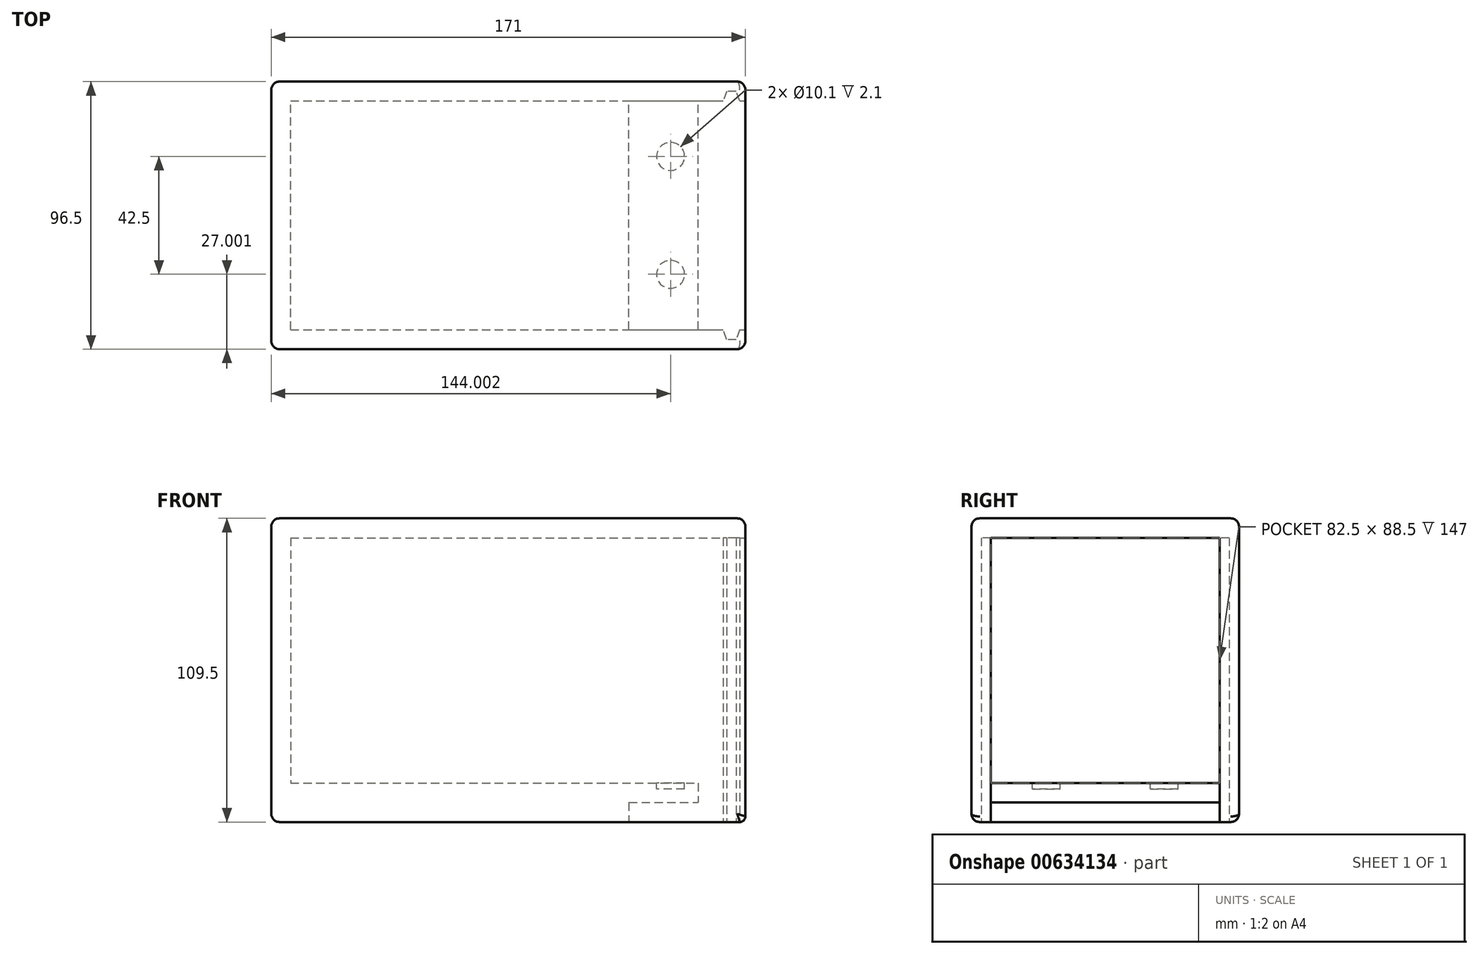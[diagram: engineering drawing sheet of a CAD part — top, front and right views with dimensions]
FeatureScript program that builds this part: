
annotation { "Feature Type Name" : "Feature", "Feature Type Description" : "" }
export const myFeature = defineFeature(function(context is Context, id is Id, definition is map)
    precondition{}
    {
        {
            var Q0;
            Q0=qCreatedBy(makeId("Top.planeOp"),FACE);
            var sketch = newSketch(context, id + "F0", { "sketchPlane" : qUnion([Q0])});
            skLineSegment(sketch, "E0.bottom", {"start": v(-82.1, 47.48) * mm, "end": v(81.9, 47.48) * mm});
            skLineSegment(sketch, "E0.top", {"start": v(-82.1, -49.02) * mm, "end": v(81.9, -49.02) * mm});
            skLineSegment(sketch, "E0.left", {"start": v(-82.1, 47.48) * mm, "end": v(-82.1, -49.02) * mm});
            skLineSegment(sketch, "E0.right", {"start": v(81.9, 47.48) * mm, "end": v(81.9, -49.02) * mm});
            skSolve(sketch);
        }
        {
            var Q0;
            Q0=makeQuery(id+"F0.imprint","IMPRINT",FACE,{"disambiguationData":[TD([[makeQuery(id+"F0.imprint","IMPRINT",EDGE,{"derivedFrom":sQuery(id+"F0.wireOp",EDGE,"E0.bottom")}),-1.0]])]});
            extrude(context, id + "F1", {"entities" : qUnion([Q0]), "depth" : 102.5 * mm, "offsetDistance" : 25 * mm});
        }
        {
            var Q0;
            Q0=makeQuery(id+"F1.opExtrude","CAP_FACE",FACE,{"disambiguationData":[OSD([sQuery(id+"F0.wireOp",EDGE,"E0.bottom"),sQuery(id+"F0.wireOp",EDGE,"E0.top"),sQuery(id+"F0.wireOp",EDGE,"E0.left"),sQuery(id+"F0.wireOp",EDGE,"E0.right")])],"isStart":false});
            var sketch = newSketch(context, id + "F2", { "sketchPlane" : qUnion([Q0])});
            skLineSegment(sketch, "E1.bottom", {"start": v(-75.1, 40.48) * mm, "end": v(74.9, 40.48) * mm});
            skLineSegment(sketch, "E1.top", {"start": v(-75.1, -42.02) * mm, "end": v(74.9, -42.02) * mm});
            skLineSegment(sketch, "E1.left", {"start": v(-75.1, 40.48) * mm, "end": v(-75.1, -42.02) * mm});
            skLineSegment(sketch, "E1.right", {"start": v(74.9, 40.48) * mm, "end": v(74.9, -42.02) * mm});
            skSolve(sketch);
        }
        {
            var Q0;
            Q0=makeQuery(id+"F1.opExtrude","SWEPT_FACE",FACE,{"disambiguationData":[OSD([sQuery(id+"F0.wireOp",EDGE,"E0.right")])]});
            var sketch = newSketch(context, id + "F3", { "sketchPlane" : qUnion([Q0])});
            skLineSegment(sketch, "E2.bottom", {"start": v(-42.02, 95.5) * mm, "end": v(40.48, 95.5) * mm});
            skLineSegment(sketch, "E2.top", {"start": v(-42.02, 7) * mm, "end": v(40.48, 7) * mm});
            skLineSegment(sketch, "E2.left", {"start": v(-42.02, 95.5) * mm, "end": v(-42.02, 7) * mm});
            skLineSegment(sketch, "E2.right", {"start": v(40.48, 95.5) * mm, "end": v(40.48, 7) * mm});
            skSolve(sketch);
        }
        {
            var Q0;
            Q0=makeQuery(id+"F3.imprint","IMPRINT",FACE,{"disambiguationData":[TD([[makeQuery(id+"F3.imprint","IMPRINT",EDGE,{"derivedFrom":sQuery(id+"F3.wireOp",EDGE,"E2.bottom")}),-1.0]])]});
            extrude(context, id + "F4", {"entities" : qUnion([Q0]), "operationType" : NewBodyOperationType.REMOVE, "oppositeDirection" : true, "depth" : 157 * mm, "offsetDistance" : 25 * mm});
        }
        {
            var Q0;
            Q0=makeQuery(id+"F1.opExtrude","CAP_FACE",FACE,{"disambiguationData":[OSD([sQuery(id+"F0.wireOp",EDGE,"E0.bottom"),sQuery(id+"F0.wireOp",EDGE,"E0.top"),sQuery(id+"F0.wireOp",EDGE,"E0.left"),sQuery(id+"F0.wireOp",EDGE,"E0.right")])],"isStart":true});
            var sketch = newSketch(context, id + "F5", { "sketchPlane" : qUnion([Q0])});
            skLineSegment(sketch, "E3.bottom", {"start": v(41.9, 42.02) * mm, "end": v(81.9, 42.02) * mm});
            skLineSegment(sketch, "E3.top", {"start": v(41.9, -40.48) * mm, "end": v(81.9, -40.48) * mm});
            skLineSegment(sketch, "E3.left", {"start": v(41.9, 42.02) * mm, "end": v(41.9, -40.48) * mm});
            skLineSegment(sketch, "E3.right", {"start": v(81.9, 42.02) * mm, "end": v(81.9, -40.48) * mm});
            skSolve(sketch);
        }
        {
            var Q0;
            Q0=makeQuery(id+"F5.imprint","IMPRINT",FACE,{"disambiguationData":[TD([[makeQuery(id+"F5.imprint","IMPRINT",EDGE,{"derivedFrom":sQuery(id+"F5.wireOp",EDGE,"E3.bottom")}),-1.0]])]});
            extrude(context, id + "F6", {"entities" : qUnion([Q0]), "operationType" : NewBodyOperationType.REMOVE, "oppositeDirection" : true, "depth" : 7 * mm, "offsetDistance" : 25 * mm});
        }
        {
            var Q0;
            Q0=makeQuery(id+"F1.opExtrude","CAP_FACE",FACE,{"disambiguationData":[OSD([sQuery(id+"F0.wireOp",EDGE,"E0.bottom"),sQuery(id+"F0.wireOp",EDGE,"E0.top"),sQuery(id+"F0.wireOp",EDGE,"E0.left"),sQuery(id+"F0.wireOp",EDGE,"E0.right")])],"isStart":true});
            extrude(context, id + "F7", {"entities" : qUnion([Q0]), "operationType" : NewBodyOperationType.ADD, "depth" : 7 * mm, "offsetDistance" : 25 * mm});
        }
        {
            var Q0;
            Q0=makeQuery(id+"F7.opExtrude","CAP_FACE",FACE,{"disambiguationData":[OSD([sQuery(id+"F0.wireOp",EDGE,"E0.bottom"),sQuery(id+"F0.wireOp",EDGE,"E0.top"),sQuery(id+"F0.wireOp",EDGE,"E0.left"),sQuery(id+"F0.wireOp",EDGE,"E0.right")])],"isStart":false});
            var sketch = newSketch(context, id + "F8", { "sketchPlane" : qUnion([Q0])});
            skLineSegment(sketch, "E4.bottom", {"start": v(11.9, 42.02) * mm, "end": v(41.9, 42.02) * mm});
            skLineSegment(sketch, "E4.top", {"start": v(11.9, -40.48) * mm, "end": v(41.9, -40.48) * mm});
            skLineSegment(sketch, "E4.left", {"start": v(11.9, 42.02) * mm, "end": v(11.9, -40.48) * mm});
            skLineSegment(sketch, "E4.right", {"start": v(41.9, 42.02) * mm, "end": v(41.9, -40.48) * mm});
            skSolve(sketch);
        }
        {
            var Q0;
            Q0=makeQuery(id+"F8.imprint","IMPRINT",FACE,{"disambiguationData":[TD([[makeQuery(id+"F8.imprint","IMPRINT",EDGE,{"derivedFrom":sQuery(id+"F8.wireOp",EDGE,"E4.bottom")}),-1.0]])]});
            extrude(context, id + "F9", {"entities" : qUnion([Q0]), "operationType" : NewBodyOperationType.REMOVE, "oppositeDirection" : true, "depth" : 7 * mm, "offsetDistance" : 25 * mm});
        }
        {
            var Q0;
            {var subQ0=sQuery(id+"F0.wireOp",EDGE,"E0.right");var subQ1=makeQuery(id+"F1.opExtrude","SWEPT_FACE",FACE,{"disambiguationData":[OSD([subQ0])]});var subQ2=sQuery(id+"F0.wireOp",EDGE,"E0.top");var subQ3=sQuery(id+"F0.wireOp",EDGE,"E0.bottom");var subQ5=makeQuery(id+"F1.opExtrude","CAP_EDGE",EDGE,{"disambiguationData":[OSD([subQ0])],"isStart":true});Q0=makeQuery(id+"F7.boolean.opBoolean","MERGE",FACE,{"derivedFrom":[subQ1,makeQuery(id+"F7.opExtrude","SWEPT_FACE",FACE,{"disambiguationData":[OSD([subQ0]),TDD([makeQuery(id+"F6.boolean.opBoolean","SPLIT",EDGE,{"disambiguationData":[TD([makeQuery(id+"F1.opExtrude","SWEPT_FACE",FACE,{"disambiguationData":[OSD([subQ3])]})])],"derivedFrom":subQ5})])]}),makeQuery(id+"F7.opExtrude","SWEPT_FACE",FACE,{"disambiguationData":[OSD([subQ0]),TDD([makeQuery(id+"F6.boolean.opBoolean","SPLIT",EDGE,{"disambiguationData":[TD([makeQuery(id+"F1.opExtrude","SWEPT_FACE",FACE,{"disambiguationData":[OSD([subQ2])]})])],"derivedFrom":subQ5})])]})]});}
            extrude(context, id + "F10", {"entities" : qUnion([Q0]), "operationType" : NewBodyOperationType.ADD, "depth" : 7 * mm, "offsetDistance" : 25 * mm});
        }
        {
            var Q0;
            {var subQ0=sQuery(id+"F0.wireOp",EDGE,"E0.right");var subQ2=sQuery(id+"F0.wireOp",EDGE,"E0.top");var subQ3=sQuery(id+"F0.wireOp",EDGE,"E0.left");var subQ4=sQuery(id+"F0.wireOp",EDGE,"E0.bottom");var subQ6=makeQuery(id+"F1.opExtrude","CAP_EDGE",EDGE,{"disambiguationData":[OSD([subQ0])],"isStart":true});Q0=makeQuery(id+"F10.boolean.opBoolean","MERGE",FACE,{"derivedFrom":[makeQuery(id+"F7.opExtrude","CAP_FACE",FACE,{"disambiguationData":[OSD([subQ4,subQ2,subQ3,subQ0])],"isStart":false}),makeQuery(id+"F10.opExtrude","SWEPT_FACE",FACE,{"disambiguationData":[OSD([subQ0]),TDD([makeQuery(id+"F7.opExtrude","CAP_EDGE",EDGE,{"disambiguationData":[OSD([subQ0]),TDD([makeQuery(id+"F6.boolean.opBoolean","SPLIT",EDGE,{"disambiguationData":[TD([makeQuery(id+"F1.opExtrude","SWEPT_FACE",FACE,{"disambiguationData":[OSD([subQ4])]})])],"derivedFrom":subQ6})])],"isStart":false})])]}),makeQuery(id+"F10.opExtrude","SWEPT_FACE",FACE,{"disambiguationData":[OSD([subQ0]),TDD([makeQuery(id+"F7.opExtrude","CAP_EDGE",EDGE,{"disambiguationData":[OSD([subQ0]),TDD([makeQuery(id+"F6.boolean.opBoolean","SPLIT",EDGE,{"disambiguationData":[TD([makeQuery(id+"F1.opExtrude","SWEPT_FACE",FACE,{"disambiguationData":[OSD([subQ2])]})])],"derivedFrom":subQ6})])],"isStart":false})])]})]});}
            var sketch = newSketch(context, id + "F11", { "sketchPlane" : qUnion([Q0])});
            skLineSegment(sketch, "E5", {"start": v(86.9, 42.02) * mm, "end": v(85.63, 45.52) * mm});
            skLineSegment(sketch, "E6", {"start": v(85.63, 45.52) * mm, "end": v(82.18, 45.52) * mm});
            skLineSegment(sketch, "E7", {"start": v(82.18, 45.52) * mm, "end": v(80.9, 42.02) * mm});
            skLineSegment(sketch, "E8", {"start": v(86.9, -40.48) * mm, "end": v(85.63, -43.98) * mm});
            skLineSegment(sketch, "E9", {"start": v(85.63, -43.98) * mm, "end": v(82.13, -43.98) * mm});
            skLineSegment(sketch, "E10", {"start": v(82.13, -43.98) * mm, "end": v(80.85, -40.48) * mm});
            skSolve(sketch);
        }
        {
            var Q0;
            {var subQ0=sQuery(id+"F11.wireOp",EDGE,"E5");Q0=makeQuery(id+"F11.imprint","IMPRINT",FACE,{"disambiguationData":[TD([[makeQuery(id+"F11.imprint","IMPRINT",EDGE,{"derivedFrom":subQ0}),1.0]])]});}
            var Q1;
            {var subQ0=sQuery(id+"F11.wireOp",EDGE,"E8");Q1=makeQuery(id+"F11.imprint","IMPRINT",FACE,{"disambiguationData":[TD([[makeQuery(id+"F11.imprint","IMPRINT",EDGE,{"derivedFrom":subQ0}),-1.0]])]});}
            extrude(context, id + "F12", {"entities" : qUnion([Q0, Q1]), "operationType" : NewBodyOperationType.REMOVE, "oppositeDirection" : true, "depth" : 102.5 * mm, "offsetDistance" : 25 * mm});
        }
        {
            var Q0;
            {var subQ0=sQuery(id+"F5.wireOp",EDGE,"E3.left");Q0=makeQuery(id+"F7.boolean.opBoolean","MERGE",FACE,{"derivedFrom":[makeQuery(id+"F6.boolean.opBoolean","COPY",FACE,{"derivedFrom":makeQuery(id+"F6.opExtrude","SWEPT_FACE",FACE,{"disambiguationData":[OSD([subQ0])]})}),makeQuery(id+"F7.opExtrude","SWEPT_FACE",FACE,{"disambiguationData":[OSD([subQ0])]})]});}
            extrude(context, id + "F13", {"entities" : qUnion([Q0]), "operationType" : NewBodyOperationType.ADD, "depth" : 30 * mm, "offsetDistance" : 25 * mm});
        }
        {
            var Q0;
            Q0=makeQuery(id+"F9.boolean.opBoolean","COPY",FACE,{"derivedFrom":makeQuery(id+"F9.opExtrude","SWEPT_FACE",FACE,{"disambiguationData":[OSD([sQuery(id+"F8.wireOp",EDGE,"E4.left")])]})});
            extrude(context, id + "F14", {"entities" : qUnion([Q0]), "operationType" : NewBodyOperationType.ADD, "depth" : 35 * mm, "offsetDistance" : 25 * mm});
        }
        {
            var Q0;
            {var subQ0=sQuery(id+"F0.wireOp",EDGE,"E0.right");var subQ1=sQuery(id+"F0.wireOp",EDGE,"E0.top");Q0=makeQuery(id+"F10.boolean.opBoolean","MERGE",EDGE,{"derivedFrom":[makeQuery(id+"F1.opExtrude","CAP_EDGE",EDGE,{"disambiguationData":[OSD([subQ1])],"isStart":false}),makeQuery(id+"F10.opExtrude","SWEPT_EDGE",EDGE,{"disambiguationData":[OSD([subQ1,subQ0]),TDD([makeQuery(id+"F1.opExtrude","CAP_VERTEX",VERTEX,{"disambiguationData":[OSD([subQ1,subQ0])],"isStart":false})])]})]});}
            var Q1;
            Q1=makeQuery(id+"F1.opExtrude","CAP_EDGE",EDGE,{"disambiguationData":[OSD([sQuery(id+"F0.wireOp",EDGE,"E0.left")])],"isStart":false});
            var Q2;
            {var subQ0=sQuery(id+"F0.wireOp",EDGE,"E0.right");var subQ1=sQuery(id+"F0.wireOp",EDGE,"E0.bottom");Q2=makeQuery(id+"F10.boolean.opBoolean","MERGE",EDGE,{"derivedFrom":[makeQuery(id+"F1.opExtrude","CAP_EDGE",EDGE,{"disambiguationData":[OSD([subQ1])],"isStart":false}),makeQuery(id+"F10.opExtrude","SWEPT_EDGE",EDGE,{"disambiguationData":[OSD([subQ1,subQ0]),TDD([makeQuery(id+"F1.opExtrude","CAP_VERTEX",VERTEX,{"disambiguationData":[OSD([subQ1,subQ0])],"isStart":false})])]})]});}
            var Q3;
            {var subQ0=sQuery(id+"F0.wireOp",EDGE,"E0.right");Q3=makeQuery(id+"F10.opExtrude","CAP_EDGE",EDGE,{"disambiguationData":[OSD([subQ0]),TDD([makeQuery(id+"F1.opExtrude","CAP_EDGE",EDGE,{"disambiguationData":[OSD([subQ0])],"isStart":false})])],"isStart":false});}
            var Q4;
            Q4=makeQuery(id+"F10.opExtrude","CAP_EDGE",EDGE,{"disambiguationData":[OSD([sQuery(id+"F0.wireOp",EDGE,"E0.top"),sQuery(id+"F0.wireOp",EDGE,"E0.right")])],"isStart":false});
            var Q5;
            Q5=makeQuery(id+"F10.opExtrude","CAP_EDGE",EDGE,{"disambiguationData":[OSD([sQuery(id+"F0.wireOp",EDGE,"E0.bottom"),sQuery(id+"F0.wireOp",EDGE,"E0.right")])],"isStart":false});
            var Q6;
            {var subQ0=sQuery(id+"F0.wireOp",EDGE,"E0.left");var subQ1=sQuery(id+"F0.wireOp",EDGE,"E0.bottom");Q6=makeQuery(id+"F7.boolean.opBoolean","MERGE",EDGE,{"derivedFrom":[makeQuery(id+"F1.opExtrude","SWEPT_EDGE",EDGE,{"disambiguationData":[OSD([subQ1,subQ0])]}),makeQuery(id+"F7.opExtrude","SWEPT_EDGE",EDGE,{"disambiguationData":[OSD([subQ1,subQ0])]})]});}
            var Q7;
            {var subQ0=sQuery(id+"F0.wireOp",EDGE,"E0.left");var subQ1=sQuery(id+"F0.wireOp",EDGE,"E0.top");Q7=makeQuery(id+"F7.boolean.opBoolean","MERGE",EDGE,{"derivedFrom":[makeQuery(id+"F1.opExtrude","SWEPT_EDGE",EDGE,{"disambiguationData":[OSD([subQ1,subQ0])]}),makeQuery(id+"F7.opExtrude","SWEPT_EDGE",EDGE,{"disambiguationData":[OSD([subQ1,subQ0])]})]});}
            var Q8;
            {var subQ0=sQuery(id+"F0.wireOp",EDGE,"E0.right");var subQ1=sQuery(id+"F0.wireOp",EDGE,"E0.bottom");Q8=makeQuery(id+"F10.boolean.opBoolean","MERGE",EDGE,{"derivedFrom":[makeQuery(id+"F7.opExtrude","CAP_EDGE",EDGE,{"disambiguationData":[OSD([subQ1])],"isStart":false}),makeQuery(id+"F10.opExtrude","SWEPT_EDGE",EDGE,{"disambiguationData":[OSD([subQ1,subQ0]),TDD([makeQuery(id+"F7.opExtrude","CAP_VERTEX",VERTEX,{"disambiguationData":[OSD([subQ1,subQ0])],"isStart":false})])]})]});}
            var Q9;
            Q9=makeQuery(id+"F7.opExtrude","CAP_EDGE",EDGE,{"disambiguationData":[OSD([sQuery(id+"F0.wireOp",EDGE,"E0.left")])],"isStart":false});
            var Q10;
            {var subQ0=sQuery(id+"F0.wireOp",EDGE,"E0.right");var subQ1=sQuery(id+"F0.wireOp",EDGE,"E0.top");Q10=makeQuery(id+"F10.boolean.opBoolean","MERGE",EDGE,{"derivedFrom":[makeQuery(id+"F7.opExtrude","CAP_EDGE",EDGE,{"disambiguationData":[OSD([subQ1])],"isStart":false}),makeQuery(id+"F10.opExtrude","SWEPT_EDGE",EDGE,{"disambiguationData":[OSD([subQ1,subQ0]),TDD([makeQuery(id+"F7.opExtrude","CAP_VERTEX",VERTEX,{"disambiguationData":[OSD([subQ1,subQ0])],"isStart":false})])]})]});}
            fillet(context, id + "F15", {"entities" : qUnion([Q0, Q1, Q2, Q3, Q4, Q5, Q6, Q7, Q8, Q9, Q10]), "radius" : 3 * mm, "tangentPropagation" : true, "allowEdgeOverflow" : false});
        }
        {
            var Q0;
            {var subQ0=sQuery(id+"F0.wireOp",EDGE,"E0.right");var subQ1=sQuery(id+"F0.wireOp",EDGE,"E0.top");Q0=makeQuery(id+"F10.opExtrude","CAP_EDGE",EDGE,{"disambiguationData":[OSD([subQ0]),TDD([makeQuery(id+"F7.opExtrude","CAP_EDGE",EDGE,{"disambiguationData":[OSD([subQ0]),TDD([makeQuery(id+"F6.boolean.opBoolean","SPLIT",EDGE,{"disambiguationData":[TD([makeQuery(id+"F1.opExtrude","SWEPT_FACE",FACE,{"disambiguationData":[OSD([subQ1])]})])],"derivedFrom":makeQuery(id+"F1.opExtrude","CAP_EDGE",EDGE,{"disambiguationData":[OSD([subQ0])],"isStart":true})})])],"isStart":false})])],"isStart":false});}
            var Q1;
            {var subQ0=sQuery(id+"F0.wireOp",EDGE,"E0.right");var subQ1=sQuery(id+"F0.wireOp",EDGE,"E0.bottom");Q1=makeQuery(id+"F10.opExtrude","CAP_EDGE",EDGE,{"disambiguationData":[OSD([subQ0]),TDD([makeQuery(id+"F7.opExtrude","CAP_EDGE",EDGE,{"disambiguationData":[OSD([subQ0]),TDD([makeQuery(id+"F6.boolean.opBoolean","SPLIT",EDGE,{"disambiguationData":[TD([makeQuery(id+"F1.opExtrude","SWEPT_FACE",FACE,{"disambiguationData":[OSD([subQ1])]})])],"derivedFrom":makeQuery(id+"F1.opExtrude","CAP_EDGE",EDGE,{"disambiguationData":[OSD([subQ0])],"isStart":true})})])],"isStart":false})])],"isStart":false});}
            fillet(context, id + "F16", {"entities" : qUnion([Q0, Q1]), "radius" : 2 * mm, "tangentPropagation" : true, "allowEdgeOverflow" : false});
        }
        {
            var Q0;
            Q0=makeQuery(id+"F13.boolean.opBoolean","MERGE",FACE,{"derivedFrom":[makeQuery(id+"F4.boolean.opBoolean","COPY",FACE,{"derivedFrom":makeQuery(id+"F4.opExtrude","SWEPT_FACE",FACE,{"disambiguationData":[OSD([sQuery(id+"F3.wireOp",EDGE,"E2.top")])]})}),makeQuery(id+"F13.opExtrude","SWEPT_FACE",FACE,{"disambiguationData":[OSD([sQuery(id+"F5.wireOp",EDGE,"E3.left")])]})]});
            var sketch = newSketch(context, id + "F17", { "sketchPlane" : qUnion([Q0])});
            skCircle(sketch, "E11", {"center": v(61.9, 20.48) * mm, "radius": 5.05 * mm});
            skCircle(sketch, "E12", {"center": v(61.9, -22.02) * mm, "radius": 5.05 * mm});
            skSolve(sketch);
        }
        {
            var Q0;
            Q0=makeQuery(id+"F17.imprint","IMPRINT",FACE,{"disambiguationData":[TD([[makeQuery(id+"F17.imprint","IMPRINT",EDGE,{"derivedFrom":sQuery(id+"F17.wireOp",EDGE,"E12")}),1.0]])]});
            var Q1;
            Q1=makeQuery(id+"F17.imprint","IMPRINT",FACE,{"disambiguationData":[TD([[makeQuery(id+"F17.imprint","IMPRINT",EDGE,{"derivedFrom":sQuery(id+"F17.wireOp",EDGE,"E11")}),1.0]])]});
            extrude(context, id + "F18", {"entities" : qUnion([Q0, Q1]), "operationType" : NewBodyOperationType.REMOVE, "oppositeDirection" : true, "depth" : 2.1 * mm, "offsetDistance" : 25 * mm});
        }
    });
